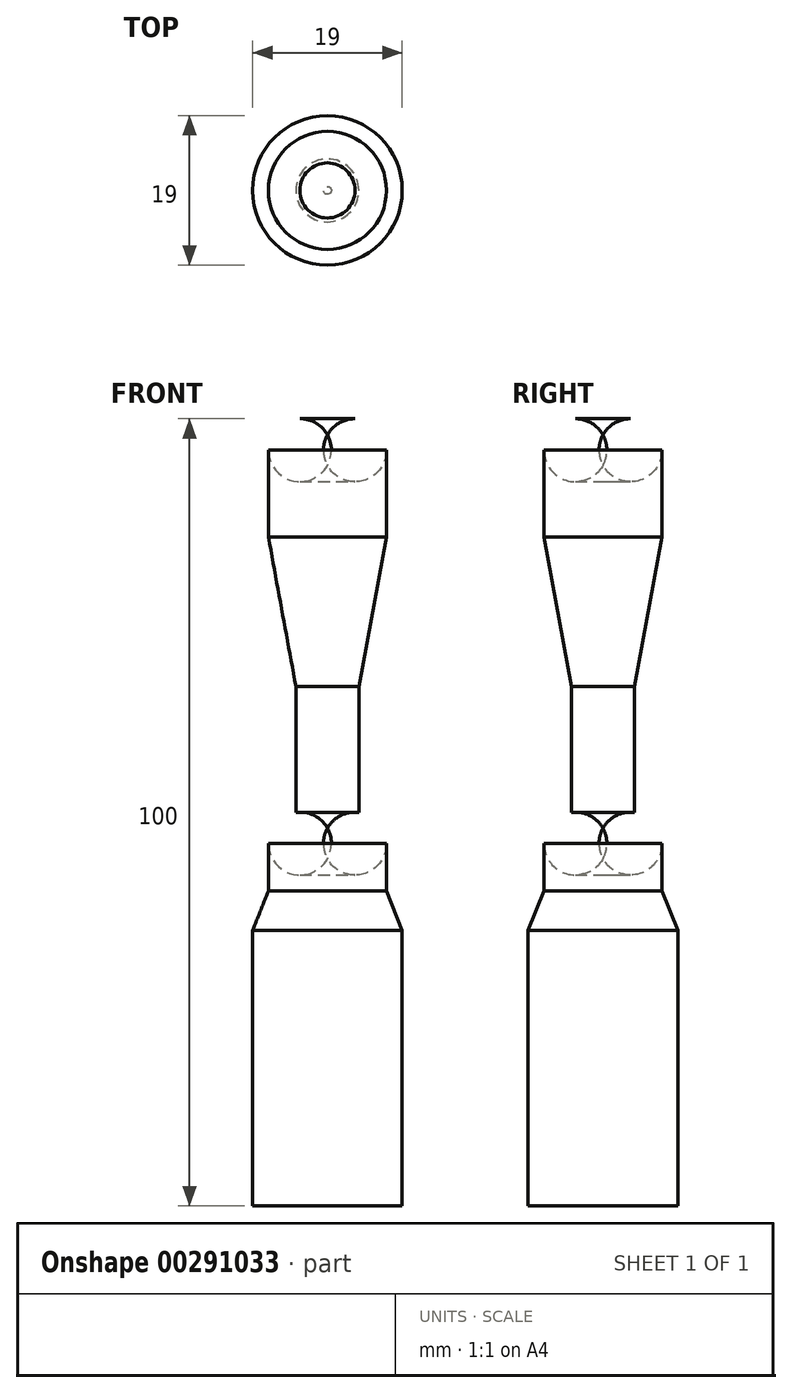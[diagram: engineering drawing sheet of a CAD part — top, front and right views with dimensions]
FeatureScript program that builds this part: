
annotation { "Feature Type Name" : "Feature", "Feature Type Description" : "" }
export const myFeature = defineFeature(function(context is Context, id is Id, definition is map)
    precondition{}
    {
        {
            var Q0;
            Q0=qCreatedBy(makeId("Front.planeOp"),FACE);
            var sketch = newSketch(context, id + "F0", { "sketchPlane" : qUnion([Q0])});
            skLineSegment(sketch, "E0", {"start": v(0, 0) * mm, "end": v(3.5, 0) * mm});
            skArc(sketch, "E1", {"start": v(7.5, -4) * mm, "mid": v(6.33, -1.17) * mm, "end": v(3.5, 0) * mm});
            skLineSegment(sketch, "E2", {"start": v(7.5, -4) * mm, "end": v(7.5, -15) * mm});
            skLineSegment(sketch, "E3", {"start": v(7.5, -15) * mm, "end": v(4, -34) * mm});
            skLineSegment(sketch, "E4", {"start": v(4, -34) * mm, "end": v(4, -50) * mm});
            skArc(sketch, "E5", {"start": v(7.5, -53.97) * mm, "mid": v(6.5, -51.32) * mm, "end": v(4, -50) * mm});
            skLineSegment(sketch, "E6", {"start": v(7.5, -53.97) * mm, "end": v(7.5, -60) * mm});
            skLineSegment(sketch, "E7", {"start": v(7.5, -60) * mm, "end": v(9.5, -65) * mm});
            skLineSegment(sketch, "E8", {"start": v(9.5, -65) * mm, "end": v(9.5, -100) * mm});
            skLineSegment(sketch, "E9", {"start": v(9.5, -100) * mm, "end": v(0, -100) * mm});
            skLineSegment(sketch, "E10", {"start": v(0, -100) * mm, "end": v(0, 0) * mm});
            skSolve(sketch);
        }
        {
            var Q0;
            Q0 = qSketchRegion(id + "F0", true);
            var Q1;
            Q1=sQuery(id+"F0.wireOp",EDGE,"E10");
            revolve(context, id + "F1", {"entities" : qUnion([Q0]), "axis" : qUnion([Q1]), "revolveType" : RevolveType.FULL});
        }
    });
